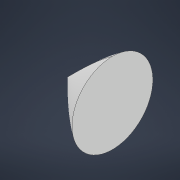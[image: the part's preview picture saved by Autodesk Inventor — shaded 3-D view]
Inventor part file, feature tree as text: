
AUTODESK INVENTOR PART (.ipt)
format: ipt  version: 2022 (Build 260153000, 153)  size: 300,032 bytes
history: native  units: in
note: dims shown in document units (in); Inventor stores cm internally (conversion verified against a paired STEP export)
features: other x2, revolve x1, sketch x1
ambient origin geometry x8: Origin, YZ Plane, XZ Plane, XY Plane, X Axis, Y Axis, Z Axis, Center Point
bodies: Body1 (feature_tree)
feature tree (4):
  revolve  "Revolution2"  Angle=90.0deg
  sketch  "Sketch1"  dims[d0=0.0in d1=1.2368in d2=0.0in d3=90.0deg d5=90.0deg]
  other  "2D Equation Curve1"
  other  "2D Equation Curve2"
